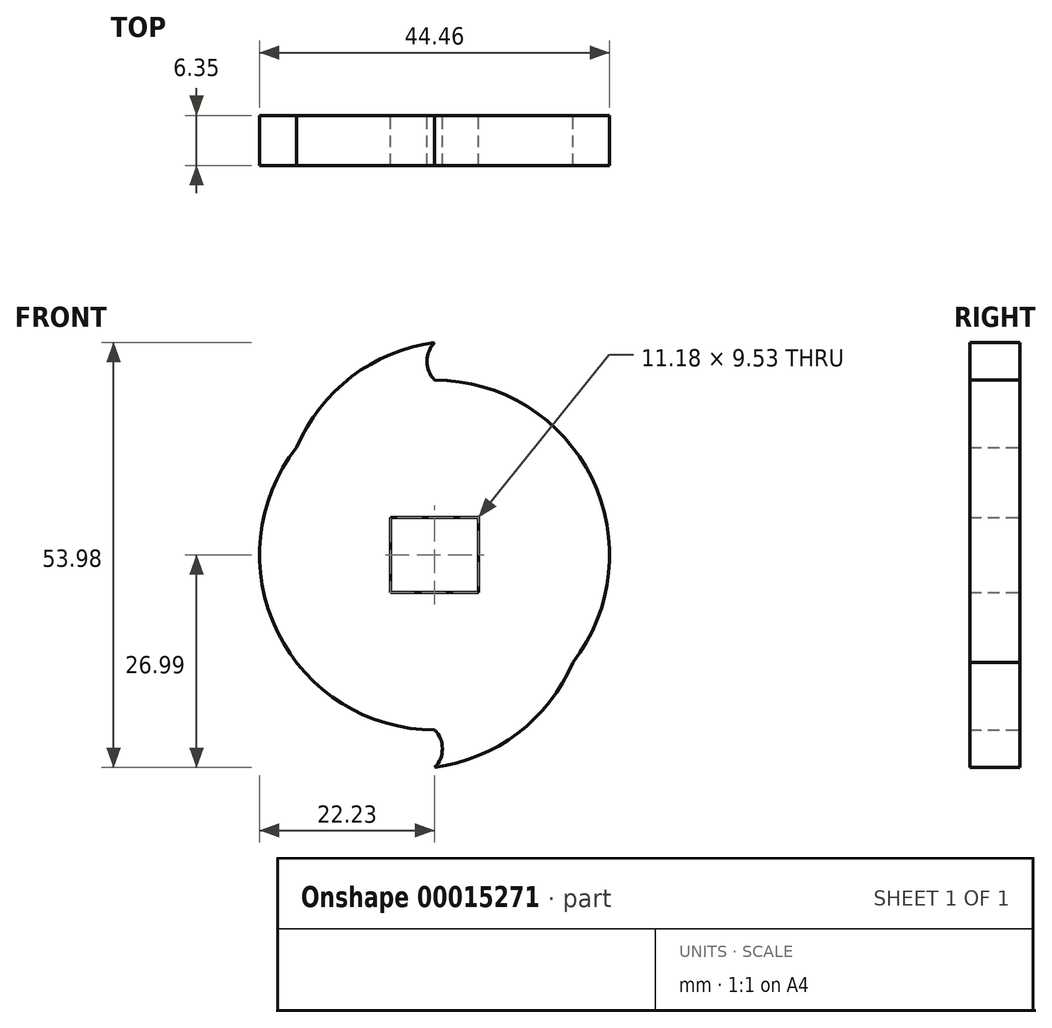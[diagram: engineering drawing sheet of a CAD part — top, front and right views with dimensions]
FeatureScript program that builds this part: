
annotation { "Feature Type Name" : "Feature", "Feature Type Description" : "" }
export const myFeature = defineFeature(function(context is Context, id is Id, definition is map)
    precondition{}
    {
        {
            var Q0;
            Q0=qCreatedBy(makeId("Front.planeOp"),FACE);
            var sketch = newSketch(context, id + "F0", { "sketchPlane" : qUnion([Q0])});
            skCircle(sketch, "E0", {"center": v(0, 0) * mm, "radius": 26.99 * mm, "construction": true});
            skArc(sketch, "E1", {"start": v(17.55, -13.64) * mm, "mid": v(19.96, 9.77) * mm, "end": v(0, 22.22) * mm});
            skArc(sketch, "E2", {"start": v(0, 26.99) * mm, "mid": v(-10.55, 22.65) * mm, "end": v(-17.55, 13.64) * mm});
            skArc(sketch, "E3", {"start": v(0, 26.99) * mm, "mid": v(-0.98, 24.6) * mm, "end": v(0, 22.23) * mm});
            skArc(sketch, "E4.1.0", {"start": v(0, -26.99) * mm, "mid": v(10.55, -22.65) * mm, "end": v(17.55, -13.64) * mm});
            skArc(sketch, "E4.1.1", {"start": v(0, -26.99) * mm, "mid": v(0.98, -24.6) * mm, "end": v(0, -22.22) * mm});
            skArc(sketch, "E5.trimOffspring", {"start": v(-17.55, 13.64) * mm, "mid": v(-19.96, -9.77) * mm, "end": v(0, -22.23) * mm});
            skLineSegment(sketch, "E6.rect.bottom", {"start": v(5.59, 4.76) * mm, "end": v(-5.59, 4.76) * mm});
            skLineSegment(sketch, "E6.rect.top", {"start": v(5.59, -4.76) * mm, "end": v(-5.59, -4.76) * mm});
            skLineSegment(sketch, "E6.rect.left", {"start": v(5.59, 4.76) * mm, "end": v(5.59, -4.76) * mm});
            skLineSegment(sketch, "E6.rect.right", {"start": v(-5.59, 4.76) * mm, "end": v(-5.59, -4.76) * mm});
            skSolve(sketch);
        }
        {
            var Q0;
            Q0=makeQuery(id+"F0.imprint","IMPRINT",FACE,{"disambiguationData":[TD([[makeQuery(id+"F0.imprint","IMPRINT",EDGE,{"derivedFrom":sQuery(id+"F0.wireOp",EDGE,"E1")}),1.0]])]});
            extrude(context, id + "F1", {"entities" : qUnion([Q0]), "depth" : 6.35 * mm});
        }
    });
